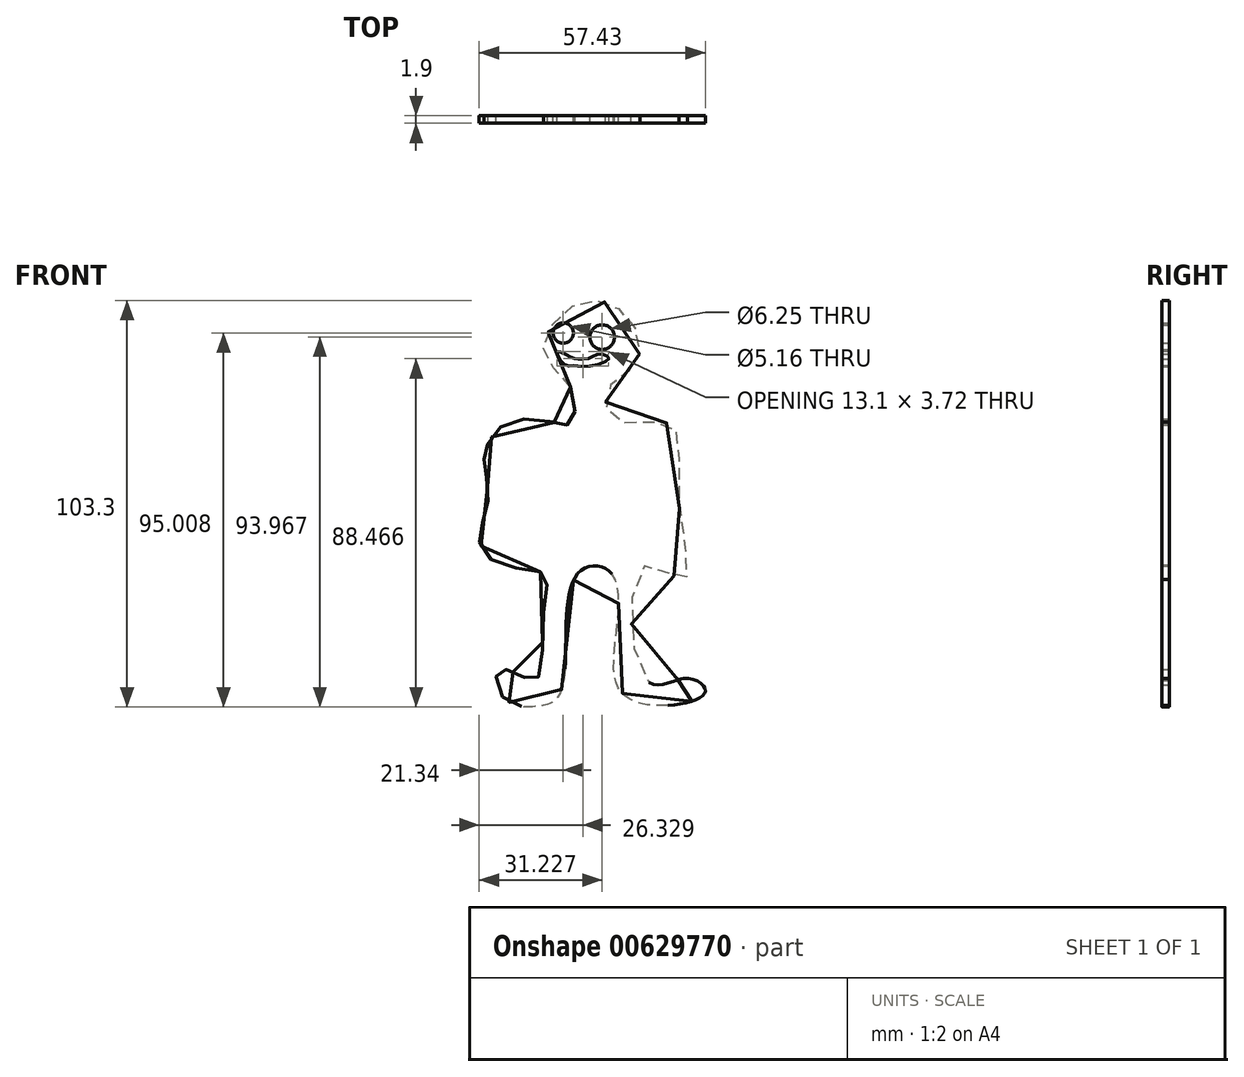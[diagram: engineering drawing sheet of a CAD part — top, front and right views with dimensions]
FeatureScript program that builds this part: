
annotation { "Feature Type Name" : "Feature", "Feature Type Description" : "" }
export const myFeature = defineFeature(function(context is Context, id is Id, definition is map)
    precondition{}
    {
        {
            var Q0;
            Q0=qCreatedBy(makeId("Front.planeOp"),FACE);
            var sketch = newSketch(context, id + "F0", { "sketchPlane" : qUnion([Q0])});
            skFitSpline(sketch, "E0", {"points": [v(-21.16, 16.04) * mm, v(-27.93, 24.2) * mm, v(-23.42, 34.6) * mm, v(-13.7, 37.9) * mm, v(-5.2, 31.66) * mm, v(-4.68, 21.94) * mm, v(-11.45, 15.87) * mm, v(-9.89, 7.72) * mm, v(4.16, 6.5) * mm, v(6.24, -12.23) * mm, v(7.46, -32.87) * mm, v(-2.6, -29.57) * mm, v(-1.9, -58.54) * mm, v(8.15, -58.02) * mm, v(13, -60.97) * mm, v(9.2, -63.92) * mm, v(-4.86, -63.92) * mm, v(-10.23, -55.6) * mm, v(-10.4, -31.83) * mm, v(-19.6, -31.66) * mm, v(-23.42, -60.62) * mm, v(-29.66, -65.13) * mm, v(-38.16, -63.05) * mm, v(-39.72, -56.29) * mm, v(-35.21, -56.63) * mm, v(-29.83, -58.2) * mm, v(-27.93, -39.64) * mm, v(-27.93, -31.48) * mm, v(-39.55, -28.88) * mm, v(-44.4, -22.12) * mm, v(-42.32, -13.96) * mm, v(-43.02, -4.08) * mm, v(-42.84, 0) * mm, v(-37.47, 6.85) * mm, v(-25.5, 7.03) * mm, v(-21.16, 6.85) * mm, v(-21.16, 16.04) * mm]});
            skCircle(sketch, "E1", {"center": v(-23.07, 29.75) * mm, "radius": 2.58 * mm});
            skCircle(sketch, "E2", {"center": v(-13.18, 28.7) * mm, "radius": 3.13 * mm});
            skFitSpline(sketch, "E3", {"points": [v(-24.63, 25.06) * mm, v(-23.07, 21.94) * mm, v(-20.47, 21.42) * mm, v(-17, 21.25) * mm, v(-11.45, 23.33) * mm, v(-13.7, 24.37) * mm, v(-16.48, 23.33) * mm, v(-19.6, 23.16) * mm, v(-21.68, 23.85) * mm, v(-24.63, 25.06) * mm]});
            skSolve(sketch);
        }
        {
            var Q0;
            Q0=makeQuery(id+"F0.imprint","IMPRINT",FACE,{"disambiguationData":[TD([[makeQuery(id+"F0.imprint","IMPRINT",EDGE,{"derivedFrom":sQuery(id+"F0.wireOp",EDGE,"E0")}),-1.0]])]});
            extrude(context, id + "F1", {"entities" : qUnion([Q0]), "depth" : 1.9 * mm, "offsetDistance" : 25 * mm});
        }
    });
